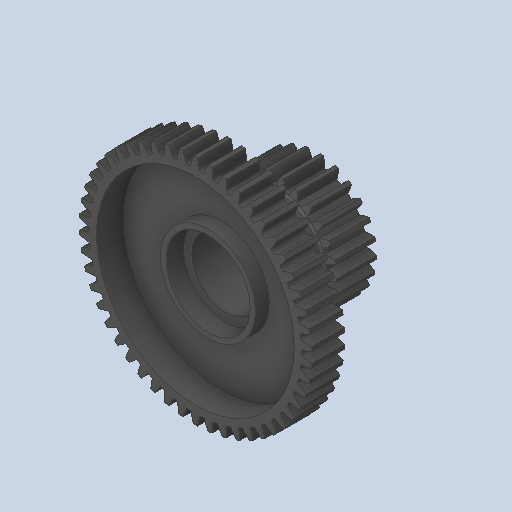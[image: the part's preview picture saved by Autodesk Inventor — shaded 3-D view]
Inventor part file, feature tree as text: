
AUTODESK INVENTOR PART (.ipt)
format: ipt  version: 2023.4 (Build 274418000, 418)  size: 571,392 bytes
history: native  units: in
note: dims shown in document units (in); Inventor stores cm internally (conversion verified against a paired STEP export)
features: chamfer x1
ambient origin geometry x8: Origin, YZ Plane, XZ Plane, XY Plane, X Axis, Y Axis, Z Axis, Center Point
bodies: Solid1 (feature_tree)
feature tree (1):
  chamfer  "Chamfer2"  [1 undecoded]
note: 1 required parameter value undecoded (feature->parameter linkage not recoverable at this tier; creation-order binding heuristic only, values carry confidence <= 0.55)
